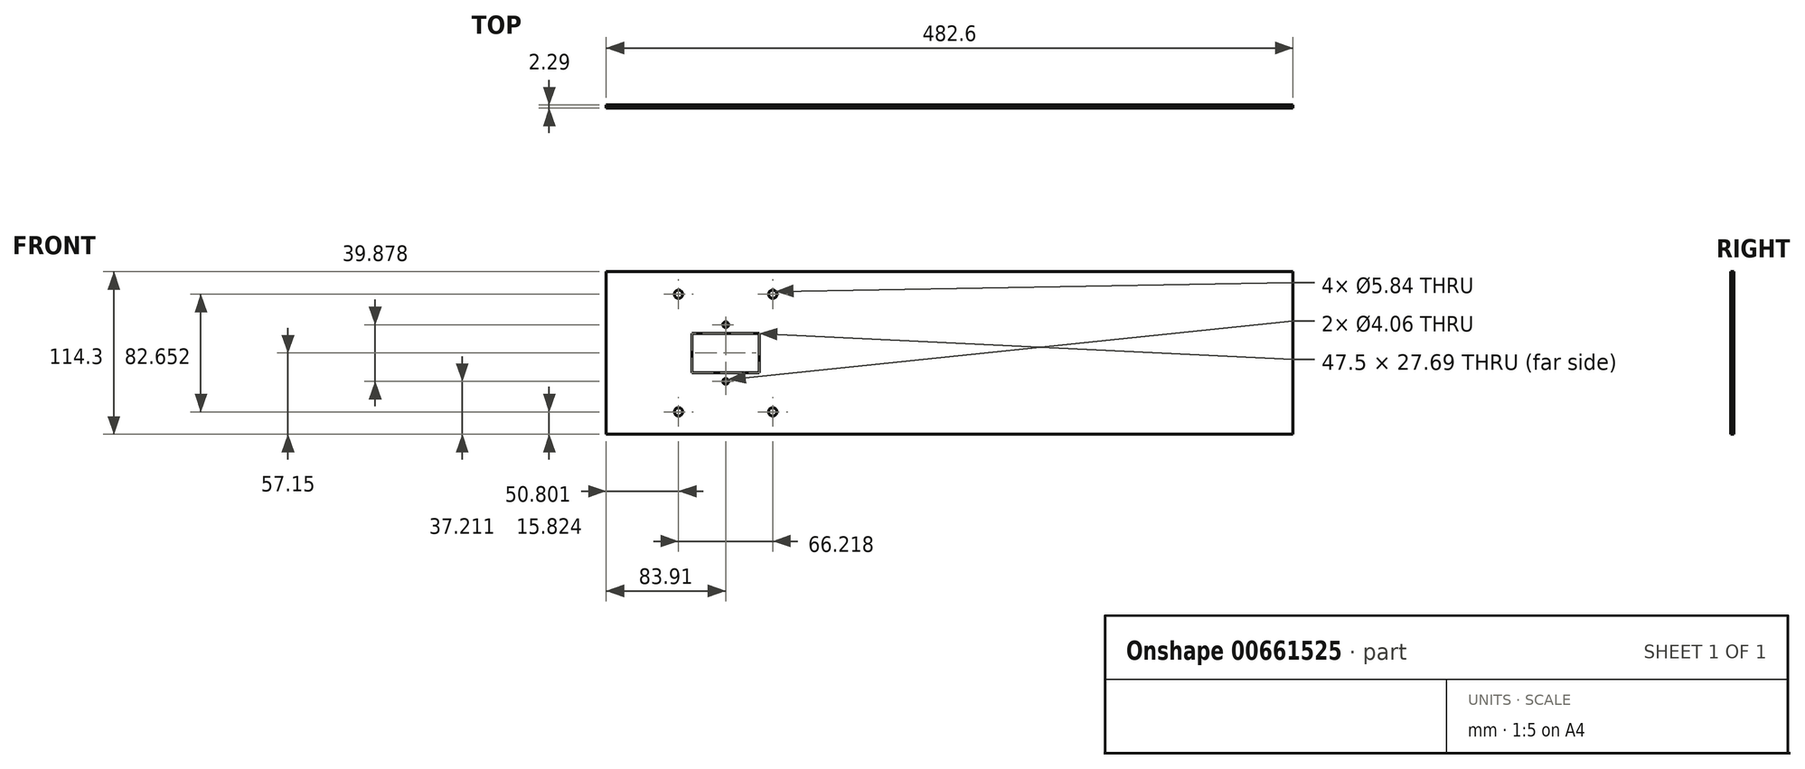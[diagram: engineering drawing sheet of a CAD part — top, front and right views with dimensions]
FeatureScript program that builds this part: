
annotation { "Feature Type Name" : "Feature", "Feature Type Description" : "" }
export const myFeature = defineFeature(function(context is Context, id is Id, definition is map)
    precondition{}
    {
        {
            var Q0;
            Q0=qCreatedBy(makeId("Front.planeOp"),FACE);
            var sketch = newSketch(context, id + "F0", { "sketchPlane" : qUnion([Q0])});
            skLineSegment(sketch, "E0.bottom", {"start": v(23.75, -13.84) * mm, "end": v(-23.75, -13.84) * mm});
            skLineSegment(sketch, "E0.top", {"start": v(23.75, 13.84) * mm, "end": v(-23.75, 13.84) * mm});
            skLineSegment(sketch, "E0.left", {"start": v(23.75, -13.84) * mm, "end": v(23.75, 13.84) * mm});
            skLineSegment(sketch, "E0.right", {"start": v(-23.75, -13.84) * mm, "end": v(-23.75, 13.84) * mm});
            skPoint(sketch, "E0.middle", {"position": v(0, 0) * mm});
            skCircle(sketch, "E1", {"center": v(0, 19.94) * mm, "radius": 2.03 * mm});
            skCircle(sketch, "E2.MirrorC", {"center": v(0, -19.94) * mm, "radius": 2.03 * mm});
            skCircle(sketch, "E3", {"center": v(-33.1, 41.33) * mm, "radius": 2.92 * mm});
            skCircle(sketch, "E4.MirrorC", {"center": v(-33.1, -41.33) * mm, "radius": 2.92 * mm});
            skCircle(sketch, "E5.MirrorC", {"center": v(33.1, 41.33) * mm, "radius": 2.92 * mm});
            skCircle(sketch, "E6.MirrorC", {"center": v(33.1, -41.33) * mm, "radius": 2.92 * mm});
            skLineSegment(sketch, "E7.bottom", {"start": v(-83.9, 57.15) * mm, "end": v(398.7, 57.15) * mm});
            skLineSegment(sketch, "E7.top", {"start": v(-83.9, -57.15) * mm, "end": v(398.7, -57.15) * mm});
            skLineSegment(sketch, "E7.left", {"start": v(-83.9, 57.15) * mm, "end": v(-83.9, -57.15) * mm});
            skLineSegment(sketch, "E7.right", {"start": v(398.7, 57.15) * mm, "end": v(398.7, -57.15) * mm});
            skPoint(sketch, "E8", {"position": v(-83.9, 0) * mm});
            skSolve(sketch);
        }
        {
            var Q0;
            Q0 = qSketchRegion(id + "F0", true);
            extrude(context, id + "F1", {"entities" : qUnion([Q0]), "depth" : 2.3 * mm, "offsetDistance" : 25.4 * mm});
        }
    });
